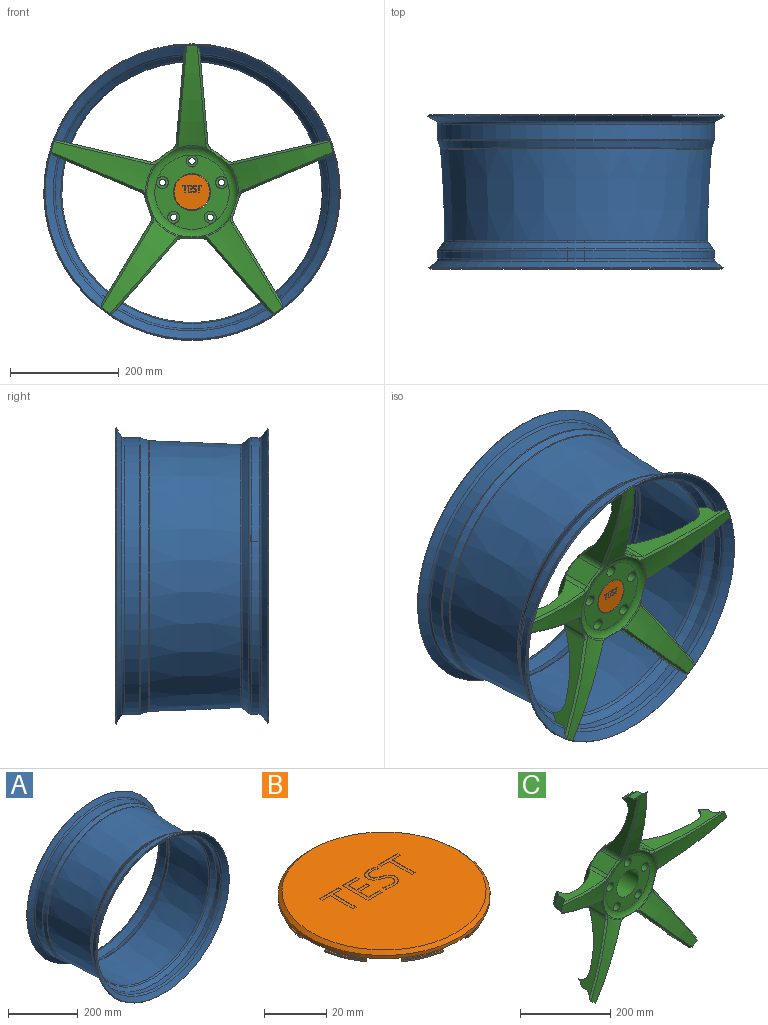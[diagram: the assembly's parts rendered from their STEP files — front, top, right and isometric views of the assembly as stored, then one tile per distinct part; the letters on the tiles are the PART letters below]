
ASSEMBLY  parts=3 mates=3
PART A: 26 faces, bbox 563.6x282.8x563.6 mm
  f0: cone r=271.25mm half-angle=52.7deg, axis (0,-1,0), area 30736.2mm2, adj f1,f25
  f1: cone r=271.25mm half-angle=37.3deg, axis (0,1,0), area 4316.6mm2, adj f0,f2
  f2: cone r=269.71mm half-angle=52.7deg, axis (0,-1,0), area 30556.8mm2, adj f1,f3
  f3: torus R=260.35mm, axis (0,1,0), area 12977.7mm2, adj f2,f4
  f4: cylinder r=251.46mm len=502.92mm, axis (0,1,0), area 24829.9mm2, adj f3,f5
  f5: cone r=251.46mm half-angle=39.7deg, axis (0,-1,0), area 24903.9mm2, adj f4,f6
  f6: torus R=248.01mm, axis (0,1,0), area 9851.6mm2, adj f5,f7
  f7: cone r=239.13mm half-angle=2.4deg, axis (0,1,0), area 255976.5mm2, adj f6,f8
  f8: torus R=255.1mm, axis (0,1,0), area 3952.3mm2, adj f7,f9
  f9: cone r=246.69mm half-angle=18.9deg, axis (0,1,0), area 23064.4mm2, adj f8,f10
  f10: cylinder r=251.46mm len=502.92mm, axis (0,1,0), area 45828.4mm2, adj f9,f11
  f11: torus R=260.35mm, axis (0,1,0), area 14328.7mm2, adj f10,f12
  f12: cone r=255.65mm half-angle=58.1deg, axis (0,1,0), area 30041.5mm2, adj f11,f13
  f13: cone r=272.41mm half-angle=31.9deg, axis (0,-1,0), area 4336.8mm2, adj f12,f14
  f14: cone r=257mm half-angle=58.1deg, axis (0,1,0), area 30194.6mm2, adj f13,f15
  f15: torus R=260.35mm, axis (0,1,0), area 10320.8mm2, adj f14,f16
  f16: cylinder r=254mm len=508mm, axis (0,1,0), area 45280.7mm2, adj f15,f17
  f17: torus R=247.65mm, axis (0,1,0), area 3336.8mm2, adj f16,f18
  f18: cone r=249.1mm half-angle=18.9deg, axis (0,1,0), area 22277.2mm2, adj f17,f19
  f19: torus R=255.1mm, axis (0,1,0), area 2851.6mm2, adj f18,f20
  f20: cone r=241.67mm half-angle=2.4deg, axis (0,1,0), area 258653.4mm2, adj f19,f21
  f21: torus R=248.01mm, axis (0,1,0), area 7105.9mm2, adj f20,f22
  f22: cone r=252.53mm half-angle=39.7deg, axis (0,-1,0), area 22913.8mm2, adj f21,f23
  f23: torus R=247.65mm, axis (0,1,0), area 7012.3mm2, adj f22,f24
  f24: cylinder r=254mm len=508mm, axis (0,1,0), area 22884.3mm2, adj f23,f25
  f25: torus R=260.35mm, axis (0,1,0), area 9350.4mm2, adj f0,f24
PART B: 117 faces, bbox 68x68x5.6 mm
  f0: plane 65.46x65.46mm, normal (0,0,1), area 3252.9mm2, adj f43,f60,f61,f62,f63,f64,f65,f66
  f1: cylinder r=32mm len=12.8mm, axis (0,0,1), area 42.1mm2, adj f2,f42,f45,f59
  f2: cone r=33.07mm half-angle=54deg, axis (0,0,1), area 18.7mm2, adj f1,f3,f45,f59
  f3: cylinder r=33.07mm len=13.22mm, axis (0,0,1), area 9.1mm2, adj f2,f4,f45,f59
  f4: plane 13.31x5.89mm, normal (0,0,1), area 7.3mm2, adj f3,f5,f45,f59
  f5: cylinder r=32.56mm len=13.02mm, axis (0,0,1), area 22.9mm2, adj f4,f42,f45,f59
  f6: cylinder r=32mm len=12.8mm, axis (0,0,1), area 42.1mm2, adj f7,f42,f56,f58
  f7: cone r=33.07mm half-angle=54deg, axis (0,0,1), area 18.7mm2, adj f6,f8,f56,f58
  f8: cylinder r=33.07mm len=13.22mm, axis (0,0,1), area 9.1mm2, adj f7,f9,f56,f58
  f9: plane 13.31x5.89mm, normal (0,0,1), area 7.3mm2, adj f8,f10,f56,f58
  f10: cylinder r=32.56mm len=13.02mm, axis (0,0,1), area 22.9mm2, adj f9,f42,f56,f58
  f11: cylinder r=32mm len=12.8mm, axis (0,0,1), area 42.1mm2, adj f12,f42,f54,f57
  f12: cone r=33.07mm half-angle=54deg, axis (0,0,1), area 18.7mm2, adj f11,f13,f54,f57
  f13: cylinder r=33.07mm len=13.22mm, axis (0,0,1), area 9.1mm2, adj f12,f14,f54,f57
  f14: plane 13.31x5.89mm, normal (0,0,1), area 7.3mm2, adj f13,f15,f54,f57
  f15: cylinder r=32.56mm len=13.02mm, axis (0,0,1), area 22.9mm2, adj f14,f42,f54,f57
  f16: cylinder r=32mm len=12.8mm, axis (0,0,1), area 42.1mm2, adj f17,f42,f52,f55
  f17: cone r=33.07mm half-angle=54deg, axis (0,0,1), area 18.7mm2, adj f16,f18,f52,f55
  f18: cylinder r=33.07mm len=13.22mm, axis (0,0,1), area 9.1mm2, adj f17,f19,f52,f55
  f19: plane 13.31x5.89mm, normal (0,0,1), area 7.3mm2, adj f18,f20,f52,f55
  f20: cylinder r=32.56mm len=13.02mm, axis (0,0,1), area 22.9mm2, adj f19,f42,f52,f55
  f21: cylinder r=32mm len=12.8mm, axis (0,0,1), area 42.1mm2, adj f22,f42,f50,f53
  f22: cone r=33.07mm half-angle=54deg, axis (0,0,1), area 18.7mm2, adj f21,f23,f50,f53
  f23: cylinder r=33.07mm len=13.22mm, axis (0,0,1), area 9.1mm2, adj f22,f24,f50,f53
  f24: plane 13.31x5.89mm, normal (0,0,1), area 7.3mm2, adj f23,f25,f50,f53
  f25: cylinder r=32.56mm len=13.02mm, axis (0,0,1), area 22.9mm2, adj f24,f42,f50,f53
  f26: cylinder r=32mm len=12.8mm, axis (0,0,1), area 42.1mm2, adj f27,f42,f48,f51
  f27: cone r=33.07mm half-angle=54deg, axis (0,0,1), area 18.7mm2, adj f26,f28,f48,f51
  f28: cylinder r=33.07mm len=13.22mm, axis (0,0,1), area 9.1mm2, adj f27,f29,f48,f51
  f29: plane 13.31x5.89mm, normal (0,0,1), area 7.3mm2, adj f28,f30,f48,f51
  f30: cylinder r=32.56mm len=13.02mm, axis (0,0,1), area 22.9mm2, adj f29,f42,f48,f51
  f31: cylinder r=32mm len=12.8mm, axis (0,0,1), area 42.1mm2, adj f32,f42,f46,f49
  f32: cone r=33.07mm half-angle=54deg, axis (0,0,1), area 18.7mm2, adj f31,f33,f46,f49
  f33: cylinder r=33.07mm len=13.22mm, axis (0,0,1), area 9.1mm2, adj f32,f34,f46,f49
  f34: plane 13.31x5.89mm, normal (0,0,1), area 7.3mm2, adj f33,f35,f46,f49
  f35: cylinder r=32.56mm len=13.02mm, axis (0,0,1), area 22.9mm2, adj f34,f42,f46,f49
  f36: cylinder r=32mm len=12.8mm, axis (0,0,1), area 42.1mm2, adj f37,f42,f44,f47
  f37: cone r=33.07mm half-angle=54deg, axis (0,0,1), area 18.7mm2, adj f36,f38,f44,f47
  f38: cylinder r=33.07mm len=13.22mm, axis (0,0,1), area 9.1mm2, adj f37,f39,f44,f47
  f39: plane 13.31x5.89mm, normal (0,0,1), area 7.3mm2, adj f38,f40,f44,f47
  f40: cylinder r=32.56mm len=13.02mm, axis (0,0,1), area 22.9mm2, adj f39,f42,f44,f47
  f41: cylinder r=34mm len=68mm, axis (0,0,-1), area 271.3mm2, adj f42,f43
  f42: plane 68x68mm, normal (0,0,-1), area 3569mm2, adj f1,f5,f6,f10,f11,f15,f16,f20
  f43: cone r=32.73mm half-angle=45deg, axis (0,0,-1), area 376.5mm2, adj f0,f41
  f44: plane 3.02x0.87mm, normal (0.57,0.82,0), area 2mm2, adj f36,f37,f38,f39,f40,f42
  f45: plane 3.02x0.87mm, normal (-0.82,-0.57,0), area 2mm2, adj f1,f2,f3,f4,f5,f42
  f46: plane 3.02x1.05mm, normal (-0.17,0.98,0), area 2mm2, adj f31,f32,f33,f34,f35,f42
  f47: plane 3.02x1.05mm, normal (-0.17,-0.98,0), area 2mm2, adj f36,f37,f38,f39,f40,f42
  f48: plane 3.02x0.87mm, normal (-0.82,0.57,0), area 2mm2, adj f26,f27,f28,f29,f30,f42
  f49: plane 3.02x0.87mm, normal (0.57,-0.82,0), area 2mm2, adj f31,f32,f33,f34,f35,f42
  f50: plane 3.02x1.05mm, normal (-0.98,-0.17,0), area 2mm2, adj f21,f22,f23,f24,f25,f42
  f51: plane 3.02x1.05mm, normal (0.98,-0.17,0), area 2mm2, adj f26,f27,f28,f29,f30,f42
  f52: plane 3.02x0.87mm, normal (-0.57,-0.82,0), area 2mm2, adj f16,f17,f18,f19,f20,f42
  f53: plane 3.02x0.87mm, normal (0.82,0.57,0), area 2mm2, adj f21,f22,f23,f24,f25,f42
  f54: plane 3.02x1.05mm, normal (0.17,-0.98,0), area 2mm2, adj f11,f12,f13,f14,f15,f42
  f55: plane 3.02x1.05mm, normal (0.17,0.98,0), area 2mm2, adj f16,f17,f18,f19,f20,f42
  f56: plane 3.02x0.87mm, normal (0.82,-0.57,0), area 2mm2, adj f6,f7,f8,f9,f10,f42
  f57: plane 3.02x0.87mm, normal (-0.57,0.82,0), area 2mm2, adj f11,f12,f13,f14,f15,f42
  f58: plane 3.02x1.05mm, normal (-0.98,0.17,0), area 2mm2, adj f6,f7,f8,f9,f10,f42
  f59: plane 3.02x1.05mm, normal (0.98,0.17,0), area 2mm2, adj f1,f2,f3,f4,f5,f42
  f60: plane 1.34x0.13mm, normal (0,1,0), area 0.2mm2, adj f0,f61,f67,f68
  f61: plane 10.35x0.13mm, normal (-1,0,0), area 1.3mm2, adj f0,f60,f62,f68
  f62: plane 3.66x0.13mm, normal (0,1,0), area 0.5mm2, adj f0,f61,f63,f68
  f63: plane 1.19x0.13mm, normal (-1,0,0), area 0.2mm2, adj f0,f62,f64,f68
  f64: plane 8.65x0.13mm, normal (0,-1,0), area 1.1mm2, adj f0,f63,f65,f68
  f65: plane 1.19x0.13mm, normal (1,0,0), area 0.2mm2, adj f0,f64,f66,f68
  f66: plane 3.66x0.13mm, normal (0,1,0), area 0.5mm2, adj f0,f65,f67,f68
  f67: plane 10.35x0.13mm, normal (1,0,0), area 1.3mm2, adj f0,f60,f66,f68
  f68: plane 11.54x8.65mm, normal (0,0,1), area 24.2mm2, adj f60,f61,f62,f63,f64,f65,f66,f67
  f69: extruded ~2.38x1.11mm, area 0.3mm2, adj f0,f70,f93,f94
  f70: extruded ~1.93x0.68mm, area 0.3mm2, adj f0,f69,f71,f94
  f71: extruded ~2.5x1.39mm, area 0.4mm2, adj f0,f70,f72,f94
  f72: extruded ~1.61x0.71mm, area 0.2mm2, adj f0,f71,f73,f94
  f73: extruded ~0.75x0.7mm, area 0.1mm2, adj f0,f72,f74,f94
  f74: extruded ~0.98x0.22mm, area 0.1mm2, adj f0,f73,f75,f94
  f75: extruded ~1.27x0.6mm, area 0.2mm2, adj f0,f74,f76,f94
  f76: extruded ~1.67x0.46mm, area 0.2mm2, adj f0,f75,f77,f94
  f77: extruded ~2.78x0.6mm, area 0.4mm2, adj f0,f76,f78,f94
  f78: plane 1.17x0.42mm, normal (-0.94,0.34,0), area 0.2mm2, adj f0,f77,f79,f94
  f79: extruded ~3.17x0.63mm, area 0.4mm2, adj f0,f78,f80,f94
  f80: extruded ~2.65x0.79mm, area 0.4mm2, adj f0,f79,f81,f94
  f81: extruded ~2.12x1mm, area 0.3mm2, adj f0,f80,f82,f94
  f82: extruded ~2.06x0.69mm, area 0.3mm2, adj f0,f81,f83,f94
  f83: extruded ~2.3x1.37mm, area 0.3mm2, adj f0,f82,f84,f94
  f84: extruded ~1.72x0.73mm, area 0.2mm2, adj f0,f83,f85,f94
  f85: extruded ~0.81x0.71mm, area 0.1mm2, adj f0,f84,f86,f94
  f86: extruded ~0.98x0.24mm, area 0.1mm2, adj f0,f85,f87,f94
  f87: extruded ~1.42x0.68mm, area 0.2mm2, adj f0,f86,f88,f94
  f88: extruded ~2.02x0.51mm, area 0.3mm2, adj f0,f87,f89,f94
  f89: extruded ~1.66x0.17mm, area 0.2mm2, adj f0,f88,f90,f94
  f90: extruded ~1.55x0.47mm, area 0.2mm2, adj f0,f89,f91,f94
  f91: plane 1.29x0.13mm, normal (1,0,0), area 0.2mm2, adj f0,f90,f92,f94
  f92: extruded ~3.16x0.53mm, area 0.4mm2, adj f0,f91,f93,f94
  f93: extruded ~3x0.85mm, area 0.4mm2, adj f0,f69,f92,f94
  f94: plane 11.87x7.26mm, normal (0,0,1), area 30.8mm2, adj f69,f70,f71,f72,f73,f74,f75,f76
  f95: plane 6.43x0.13mm, normal (0,1,0), area 0.8mm2, adj f0,f96,f106,f107
  f96: plane 1.2x0.13mm, normal (-1,0,0), area 0.2mm2, adj f0,f95,f97,f107
  f97: plane 5.09x0.13mm, normal (0,-1,0), area 0.6mm2, adj f0,f96,f98,f107
  f98: plane 4.25x0.13mm, normal (-1,0,0), area 0.5mm2, adj f0,f97,f99,f107
  f99: plane 4.78x0.13mm, normal (0,1,0), area 0.6mm2, adj f0,f98,f100,f107
  f100: plane 1.19x0.13mm, normal (-1,0,0), area 0.2mm2, adj f0,f99,f101,f107
  f101: plane 4.78x0.13mm, normal (0,-1,0), area 0.6mm2, adj f0,f100,f102,f107
  f102: plane 3.72x0.13mm, normal (-1,0,0), area 0.5mm2, adj f0,f101,f103,f107
  f103: plane 5.09x0.13mm, normal (0,1,0), area 0.6mm2, adj f0,f102,f104,f107
  f104: plane 1.19x0.13mm, normal (-1,0,0), area 0.2mm2, adj f0,f103,f105,f107
  f105: plane 6.43x0.13mm, normal (0,-1,0), area 0.8mm2, adj f0,f104,f106,f107
  f106: plane 11.54x0.13mm, normal (1,0,0), area 1.5mm2, adj f0,f95,f105,f107
  f107: plane 11.54x6.43mm, normal (0,0,1), area 33.3mm2, adj f95,f96,f97,f98,f99,f100,f101,f102
  f108: plane 1.34x0.13mm, normal (0,1,0), area 0.2mm2, adj f0,f109,f115,f116
  f109: plane 10.35x0.13mm, normal (-1,0,0), area 1.3mm2, adj f0,f108,f110,f116
  f110: plane 3.66x0.13mm, normal (0,1,0), area 0.5mm2, adj f0,f109,f111,f116
  f111: plane 1.19x0.13mm, normal (-1,0,0), area 0.2mm2, adj f0,f110,f112,f116
  f112: plane 8.65x0.13mm, normal (0,-1,0), area 1.1mm2, adj f0,f111,f113,f116
  f113: plane 1.19x0.13mm, normal (1,0,0), area 0.2mm2, adj f0,f112,f114,f116
  f114: plane 3.66x0.13mm, normal (0,1,0), area 0.5mm2, adj f0,f113,f115,f116
  f115: plane 10.35x0.13mm, normal (1,0,0), area 1.3mm2, adj f0,f108,f114,f116
  f116: plane 11.54x8.65mm, normal (0,0,1), area 24.2mm2, adj f108,f109,f110,f111,f112,f113,f114,f115
PART C: 115 faces, bbox 563.4x265.7x563.2 mm
  f0: cylinder r=6mm len=30.56mm, axis (0,-1,0), area 1152.1mm2, adj f1,f114
  f1: plane 22x22mm, normal (0,-1,0), area 267mm2, adj f0,f2
  f2: cylinder r=11mm len=25.4mm, axis (0,-1,0), area 1755.5mm2, adj f1,f3
  f3: plane 136.4x136.4mm, normal (0,-1,0), area 9079.9mm2, adj f2,f4,f7,f10,f13,f16,f113
  f4: cylinder r=11mm len=25.4mm, axis (0,-1,0), area 1755.5mm2, adj f3,f5
  f5: plane 22x22mm, normal (0,-1,0), area 267mm2, adj f4,f6
  f6: cylinder r=6mm len=30.56mm, axis (0,-1,0), area 1152.1mm2, adj f5,f114
  f7: cylinder r=11mm len=25.4mm, axis (0,-1,0), area 1755.5mm2, adj f3,f8
  f8: plane 22x22mm, normal (0,-1,0), area 267mm2, adj f7,f9
  f9: cylinder r=6mm len=30.56mm, axis (0,-1,0), area 1152.1mm2, adj f8,f114
  f10: cylinder r=11mm len=25.4mm, axis (0,-1,0), area 1755.5mm2, adj f3,f11
  f11: plane 22x22mm, normal (0,-1,0), area 267mm2, adj f10,f12
  f12: cylinder r=6mm len=30.56mm, axis (0,-1,0), area 1152.1mm2, adj f11,f114
  f13: cylinder r=11mm len=25.4mm, axis (0,-1,0), area 1755.5mm2, adj f3,f14
  f14: plane 46x46mm, normal (0,-1,0), area 267mm2, adj f13,f15
  f15: cylinder r=6mm len=30.56mm, axis (0,-1,0), area 2304.1mm2, adj f14,f114
  f16: torus R=68.2mm, axis (0,-1,0), area 7761.4mm2, adj f3,f17,f99,f100,f101,f102,f103,f104
  f17: bspline ~20.44x5.09mm, area 96.1mm2, adj f16,f18,f98,f99,f112
  f18: bspline ~12.29x9.4mm, area 74.4mm2, adj f17,f19,f96,f97,f99
  f19: bspline ~140.43x121.51mm, area 996.2mm2, adj f18,f20,f95,f97
  f20: plane 133.93x116.73mm, normal (-0.75,0,-0.66), area 4539mm2, adj f19,f21,f90,f91,f92,f93,f94,f95
  f21: torus R=260.35mm, axis (0,-1,0), area 245mm2, adj f20,f22,f90,f95
  f22: plane 151.8x92.14mm, normal (0.86,0,0.52), area 4539mm2, adj f21,f23,f25,f90,f91,f92,f93,f94
  f23: bspline ~156.96x97.56mm, area 996.2mm2, adj f22,f24,f95,f97
  f24: bspline ~13.46x7.35mm, area 74.4mm2, adj f23,f25,f97,f99,f100
  f25: cylinder r=12.7mm len=56.68mm, axis (0,1,0), area 557.4mm2, adj f22,f24,f26,f94
  f26: plane 56.13x37.22mm, normal (0.95,0,-0.31), area 2122.6mm2, adj f25,f27,f94,f100,f101
  f27: cylinder r=12.7mm len=56.68mm, axis (0,1,0), area 557.4mm2, adj f26,f28,f89,f94
  f28: plane 162.84x91.52mm, normal (0.39,0,-0.92), area 4539mm2, adj f27,f29,f83,f84,f85,f86,f87,f88
  f29: torus R=260.35mm, axis (0,-1,0), area 245mm2, adj f28,f30,f83,f88
  f30: plane 172.24x91.52mm, normal (-0.22,0,0.97), area 4539mm2, adj f29,f31,f34,f83,f84,f85,f86,f88
  f31: bspline ~177.26x45.14mm, area 996.2mm2, adj f30,f32,f33,f88
  f32: bspline ~13.53x7.55mm, area 74.4mm2, adj f31,f33,f34,f102,f103
  f33: torus R=350.52mm, axis (0,-1,0), area 6800.4mm2, adj f31,f32,f87,f88,f89,f102
  f34: cylinder r=12.7mm len=56.68mm, axis (0,1,0), area 557.4mm2, adj f30,f32,f35,f94
  f35: plane 56.13x31.69mm, normal (0.59,0,0.81), area 2122.6mm2, adj f34,f36,f94,f103,f104
  f36: cylinder r=12.7mm len=56.68mm, axis (0,1,0), area 557.4mm2, adj f35,f37,f82,f94
  f37: plane 176.04x91.52mm, normal (1,0,0.09), area 4539mm2, adj f36,f38,f76,f77,f78,f79,f80,f81
  f38: torus R=260.35mm, axis (0,-1,0), area 245mm2, adj f37,f39,f76,f81
  f39: plane 176.04x91.52mm, normal (-1,0,0.09), area 4539mm2, adj f38,f40,f43,f76,f77,f78,f79,f81
  f40: bspline ~182.08x44.43mm, area 996.2mm2, adj f39,f41,f42,f81
  f41: bspline ~13.42x9.28mm, area 74.4mm2, adj f40,f42,f43,f105,f106
  f42: torus R=350.52mm, axis (0,-1,0), area 6800.4mm2, adj f40,f41,f80,f81,f82,f105
  f43: cylinder r=12.7mm len=56.68mm, axis (0,1,0), area 557.4mm2, adj f39,f41,f44,f94
  f44: plane 56.13x31.69mm, normal (-0.59,0,0.81), area 2122.6mm2, adj f43,f45,f94,f106,f107
  f45: cylinder r=12.7mm len=56.68mm, axis (0,1,0), area 557.4mm2, adj f44,f46,f75,f94
  f46: plane 172.24x91.52mm, normal (0.22,0,0.97), area 4539mm2, adj f45,f47,f69,f70,f71,f72,f73,f74
  f47: torus R=260.35mm, axis (0,-1,0), area 245mm2, adj f46,f48,f69,f74
  f48: plane 162.84x91.52mm, normal (-0.39,0,-0.92), area 4539mm2, adj f47,f49,f52,f69,f70,f71,f72,f74
  f49: bspline ~178.01x77.76mm, area 996.2mm2, adj f48,f50,f51,f74
  f50: bspline ~12x11.18mm, area 74.4mm2, adj f49,f51,f52,f108,f109
  f51: torus R=350.52mm, axis (0,-1,0), area 6800.4mm2, adj f49,f50,f73,f74,f75,f108
  f52: cylinder r=12.7mm len=56.68mm, axis (0,1,0), area 557.4mm2, adj f48,f50,f53,f94
  f53: plane 56.13x37.22mm, normal (-0.95,0,-0.31), area 2122.6mm2, adj f52,f54,f94,f109,f110
  f54: cylinder r=12.7mm len=56.68mm, axis (0,1,0), area 557.4mm2, adj f53,f55,f68,f94
  f55: plane 151.8x92.14mm, normal (-0.86,0,0.52), area 4539mm2, adj f54,f56,f62,f63,f64,f65,f66,f67
  f56: torus R=260.35mm, axis (0,-1,0), area 245mm2, adj f55,f57,f62,f67
  f57: plane 133.93x116.73mm, normal (0.75,0,-0.66), area 4539mm2, adj f56,f58,f61,f62,f63,f64,f65,f67
  f58: bspline ~140.43x121.51mm, area 996.2mm2, adj f57,f59,f60,f67
  f59: bspline ~12.29x9.4mm, area 74.4mm2, adj f58,f60,f61,f111,f112
  f60: torus R=350.52mm, axis (0,-1,0), area 6800.4mm2, adj f58,f59,f66,f67,f68,f111
  f61: cylinder r=12.7mm len=56.68mm, axis (0,1,0), area 557.4mm2, adj f57,f59,f94,f98
  f62: cylinder r=251.46mm len=24.53mm, axis (0,-1,0), area 476.8mm2, adj f55,f56,f57,f63
  f63: cone r=251.46mm half-angle=39.7deg, axis (0,-1,0), area 503.1mm2, adj f55,f57,f62,f64
  f64: torus R=248.01mm, axis (0,-1,0), area 211.9mm2, adj f55,f57,f63,f65
  f65: torus R=216.22mm, axis (0,-1,0), area 1386.1mm2, adj f55,f57,f64,f94
  f66: bspline ~156.96x97.56mm, area 996.2mm2, adj f55,f60,f67,f68
  f67: cone r=269.71mm half-angle=52.7deg, axis (0,-1,0), area 498.8mm2, adj f55,f56,f57,f58,f60,f66
  f68: bspline ~13.46x7.35mm, area 74.4mm2, adj f54,f60,f66,f110,f111
  f69: cylinder r=251.46mm len=28.83mm, axis (0,-1,0), area 476.8mm2, adj f46,f47,f48,f70
  f70: cone r=251.46mm half-angle=39.7deg, axis (0,-1,0), area 503.1mm2, adj f46,f48,f69,f71
  f71: torus R=248.01mm, axis (0,-1,0), area 211.9mm2, adj f46,f48,f70,f72
  f72: torus R=216.22mm, axis (0,-1,0), area 1386.1mm2, adj f46,f48,f71,f94
  f73: bspline ~177.26x45.14mm, area 996.2mm2, adj f46,f51,f74,f75
  f74: cone r=269.71mm half-angle=52.7deg, axis (0,-1,0), area 498.8mm2, adj f46,f47,f48,f49,f51,f73
  f75: bspline ~13.53x6.92mm, area 74.4mm2, adj f45,f51,f73,f107,f108
  f76: cylinder r=251.46mm len=30.32mm, axis (0,-1,0), area 476.8mm2, adj f37,f38,f39,f77
  f77: cone r=251.46mm half-angle=39.7deg, axis (0,-1,0), area 503.1mm2, adj f37,f39,f76,f78
  f78: torus R=248.01mm, axis (0,-1,0), area 211.9mm2, adj f37,f39,f77,f79
  f79: torus R=216.22mm, axis (0,-1,0), area 1386.1mm2, adj f37,f39,f78,f94
  f80: bspline ~182.08x44.43mm, area 996.2mm2, adj f37,f42,f81,f82
  f81: cone r=269.71mm half-angle=52.7deg, axis (0,-1,0), area 498.8mm2, adj f37,f38,f39,f40,f42,f80
  f82: bspline ~13.42x9.28mm, area 74.4mm2, adj f36,f42,f80,f104,f105
  f83: cylinder r=251.46mm len=28.83mm, axis (0,-1,0), area 476.8mm2, adj f28,f29,f30,f84
  f84: cone r=251.46mm half-angle=39.7deg, axis (0,-1,0), area 503.1mm2, adj f28,f30,f83,f85
  f85: torus R=248.01mm, axis (0,-1,0), area 211.9mm2, adj f28,f30,f84,f86
  f86: torus R=216.22mm, axis (0,-1,0), area 1386.1mm2, adj f28,f30,f85,f94
  f87: bspline ~169.56x74.16mm, area 996.2mm2, adj f28,f33,f88,f89
  f88: cone r=269.71mm half-angle=52.7deg, axis (0,-1,0), area 498.8mm2, adj f28,f29,f30,f31,f33,f87
  f89: bspline ~12x11.18mm, area 74.4mm2, adj f27,f33,f87,f101,f102
  f90: cylinder r=251.46mm len=24.53mm, axis (0,-1,0), area 476.8mm2, adj f20,f21,f22,f91
  f91: cone r=251.46mm half-angle=39.7deg, axis (0,-1,0), area 503.1mm2, adj f20,f22,f90,f92
  f92: torus R=248.01mm, axis (0,-1,0), area 211.9mm2, adj f20,f22,f91,f93
  f93: torus R=216.22mm, axis (0,-1,0), area 1386.1mm2, adj f20,f22,f92,f94
  f94: torus R=248.49mm, axis (0,-1,0), area 40187.1mm2, adj f20,f22,f25,f26,f27,f28,f30,f34
  f95: cone r=269.71mm half-angle=52.7deg, axis (0,-1,0), area 498.8mm2, adj f19,f20,f21,f22,f23,f97
  f96: cylinder r=12.7mm len=56.68mm, axis (0,1,0), area 557.4mm2, adj f18,f20,f94,f98
  f97: torus R=350.52mm, axis (0,-1,0), area 6800.4mm2, adj f18,f19,f23,f24,f95,f99
  f98: plane 57.62x40.62mm, normal (0,0,-1), area 2122.6mm2, adj f17,f61,f94,f96,f112
  f99: torus R=87.63mm, axis (0,-1,0), area 181mm2, adj f16,f17,f18,f24,f97,f100
  f100: bspline ~19.92x10.2mm, area 96.1mm2, adj f16,f24,f26,f99,f101
  f101: bspline ~19.65x10.32mm, area 96.1mm2, adj f16,f26,f89,f100,f102
  f102: torus R=87.63mm, axis (0,-1,0), area 181mm2, adj f16,f32,f33,f89,f101,f103
  f103: bspline ~19.51x15.91mm, area 96.1mm2, adj f16,f32,f35,f102,f104
  f104: bspline ~19.25x16.12mm, area 96.1mm2, adj f16,f35,f82,f103,f105
  f105: torus R=87.63mm, axis (0,-1,0), area 181mm2, adj f16,f41,f42,f82,f104,f106
  f106: bspline ~19.25x16.12mm, area 96.1mm2, adj f16,f41,f44,f105,f107
  f107: bspline ~19.51x15.91mm, area 96.1mm2, adj f16,f44,f75,f106,f108
  f108: torus R=87.63mm, axis (0,-1,0), area 181mm2, adj f16,f50,f51,f75,f107,f109
  f109: bspline ~19.65x10.32mm, area 96.1mm2, adj f16,f50,f53,f108,f110
  f110: bspline ~19.92x10.2mm, area 96.1mm2, adj f16,f53,f68,f109,f111
  f111: torus R=87.63mm, axis (0,-1,0), area 181mm2, adj f16,f59,f60,f68,f110,f112
  f112: bspline ~20.44x5.09mm, area 96.1mm2, adj f16,f17,f59,f98,f111
  f113: cylinder r=34mm len=68mm, axis (0,-1,0), area 11954.5mm2, adj f3,f114
  f114: plane 165.1x165.1mm, normal (0,1,0), area 17211.2mm2, adj f0,f6,f9,f12,f15,f94,f113
PLACE A t=(7.81,95.17,0.63)mm
PLACE B rot(axis=(1,0,0),90deg) t=(7.81,6.75,0.86)mm
PLACE C t=(7.81,95.17,0.63)mm
MATE fastened B.f0 <-> C.f16  axis (0,-1,0) through (7.81,4.21,0.63)mm
MATE cylindrical C.f16 <-> A.f0  axis (0,-1,0) through (7.81,32.19,0.63)mm
MATE fastened A.f0 <-> C.f16  axis (0,-1,0) through (7.81,-6.79,0.63)mm
